# Revit family: Sink-Undermount-Lavatory-KALLISTA-Citizen-P20264
name_source: partatom
category: Plumbing Fixtures
units: mm (PartAtom-declared; Revit-internal decimal feet)

## family parameters
Cut with Voids When Loaded = No
Host = Face
Maintain Annotation Orientation = No
OmniClass Number = 23.31.13.00
OmniClass Title = Sinks
Part Type = Normal
Room Calculation Point = No
Round Connector Dimension = Use Diameter
Shared = No

## types (2) — shared parameters
ADA Compliant = Yes
Assembly Code = D2010400
CW Connection = No
Cold Water Inlet = Cold Water Inlet
Date Modified = 05/09/2025
Default Elevation = 36"
Description = Large Under mount Sink with Overflow
Drain Included = No
HW Connection = No
Height = 7 3/8"
Hot Water Inlet = Hot Water Inlet
Length = 21 1/8"
Manufacturer = Kallista  Co.
Master Format 2014 = 22 41 16
Master Format 2014 Name = Residential Lavatories and Sinks
Material = Premium Metal Construction
Product Name = Undermount Lavatory
URL = https://www.kallista.com
Vent Connection = No
Waste Connection = Yes
Waste Water Outlet = Waste Water Outlet
WaterSense Certified = No
Width = 17 1/4"

## per-type parameters (varying)
| type | Finish | Model | Product Documentation Link | Product Page URL | Type |
| 0-White | Kallista-Vitreous_China-0-White | P20264-00-0 | https://techcomm.kohler.com | https://www.kallista.com | 1 |
| 96-Biscuit | Kallista-Vitreous_China-96-Biscuit | P20264-00-96 |  |  | 2 |

## geometry (parser evidence)
native form markers: Sweep x6
no freeform markers — native parametric forms only
